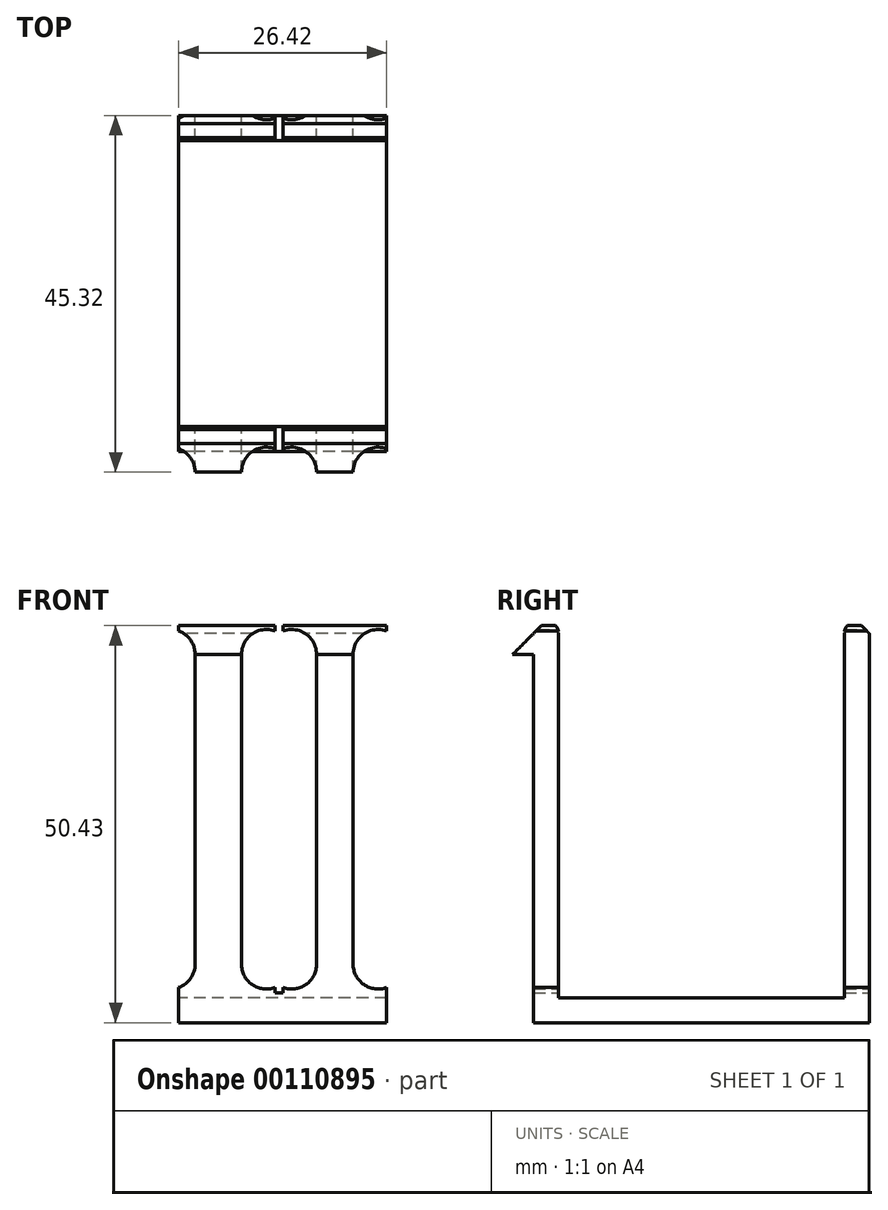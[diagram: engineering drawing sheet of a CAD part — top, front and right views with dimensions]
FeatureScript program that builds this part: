
annotation { "Feature Type Name" : "Feature", "Feature Type Description" : "" }
export const myFeature = defineFeature(function(context is Context, id is Id, definition is map)
    precondition{}
    {
        {
            var Q0;
            Q0=qCreatedBy(makeId("Right.planeOp"),FACE);
            var sketch = newSketch(context, id + "F0", { "sketchPlane" : qUnion([Q0])});
            skLineSegment(sketch, "E0", {"start": v(0, 49.53) * mm, "end": v(2.17, 50.43) * mm});
            skLineSegment(sketch, "E1", {"start": v(2.17, 50.43) * mm, "end": v(5.82, 46.78) * mm});
            skLineSegment(sketch, "E2", {"start": v(5.82, 46.78) * mm, "end": v(3.17, 46.78) * mm});
            skLineSegment(sketch, "E3", {"start": v(3.17, 46.78) * mm, "end": v(3.18, 0) * mm});
            skLineSegment(sketch, "E4", {"start": v(3.18, 0) * mm, "end": v(-18.16, 0) * mm});
            skLineSegment(sketch, "E5", {"start": v(-18.16, 0) * mm, "end": v(-18.16, 3.17) * mm});
            skLineSegment(sketch, "E6", {"start": v(-18.16, 3.17) * mm, "end": v(0, 3.17) * mm});
            skLineSegment(sketch, "E7", {"start": v(0, 3.18) * mm, "end": v(0, 49.53) * mm});
            skArc(sketch, "E8", {"start": v(2.17, 50.43) * mm, "mid": v(0.78, 50.7) * mm, "end": v(0, 49.53) * mm});
            skLineSegment(sketch, "E9.MirrorCS", {"start": v(-36.32, 49.53) * mm, "end": v(-38.5, 50.43) * mm});
            skArc(sketch, "E10.MirrorCS", {"start": v(-38.5, 50.43) * mm, "mid": v(-37.1, 50.7) * mm, "end": v(-36.32, 49.53) * mm});
            skLineSegment(sketch, "E11.MirrorCS", {"start": v(-36.32, 3.18) * mm, "end": v(-36.32, 49.53) * mm});
            skLineSegment(sketch, "E12.MirrorCS", {"start": v(-39.5, 46.78) * mm, "end": v(-39.5, 0) * mm});
            skLineSegment(sketch, "E13.MirrorCS", {"start": v(-18.16, 3.17) * mm, "end": v(-36.32, 3.17) * mm});
            skLineSegment(sketch, "E14.MirrorCS", {"start": v(-39.5, 0) * mm, "end": v(-18.16, 0) * mm});
            skLineSegment(sketch, "E15.MirrorCS", {"start": v(-38.5, 50.43) * mm, "end": v(-42.14, 46.78) * mm});
            skLineSegment(sketch, "E16.MirrorCS", {"start": v(-42.14, 46.78) * mm, "end": v(-39.5, 46.78) * mm});
            skSolve(sketch);
        }
        {
            var Q0;
            Q0 = qSketchRegion(id + "F0", true);
            extrude(context, id + "F1", {"entities" : qUnion([Q0]), "depth" : 191 * mm});
        }
        {
            var Q0;
            Q0=makeQuery(id+"F1.opExtrude","SWEPT_FACE",FACE,{"disambiguationData":[OSD([sQuery(id+"F0.wireOp",EDGE,"E3")])]});
            var sketch = newSketch(context, id + "F2", { "sketchPlane" : qUnion([Q0])});
            skLineSegment(sketch, "E17", {"start": v(0, 0) * mm, "end": v(-26.42, 0) * mm});
            skLineSegment(sketch, "E18", {"start": v(-26.42, 0) * mm, "end": v(0, 0) * mm});
            skLineSegment(sketch, "E19", {"start": v(0, 0) * mm, "end": v(0, 4.47) * mm});
            skLineSegment(sketch, "E20", {"start": v(-2.08, 7.45) * mm, "end": v(-2.08, 46.78) * mm});
            skLineSegment(sketch, "E21", {"start": v(-7.96, 7.45) * mm, "end": v(-7.96, 46.78) * mm});
            skLineSegment(sketch, "E22", {"start": v(-17.52, 7.45) * mm, "end": v(-17.52, 46.78) * mm});
            skLineSegment(sketch, "E23", {"start": v(-22.15, 7.45) * mm, "end": v(-22.15, 46.78) * mm});
            skArc(sketch, "E24", {"start": v(-2.08, 7.45) * mm, "mid": v(-1.5, 5.63) * mm, "end": v(0, 4.47) * mm});
            skArc(sketch, "E25", {"start": v(-26.42, 4.47) * mm, "mid": v(-23.5, 4.84) * mm, "end": v(-22.15, 7.45) * mm});
            skLineSegment(sketch, "E26", {"start": v(-26.42, 4.47) * mm, "end": v(-26.42, 0) * mm});
            skLineSegment(sketch, "E27", {"start": v(-13.25, 4.47) * mm, "end": v(-13.25, 3.8) * mm});
            skLineSegment(sketch, "E28", {"start": v(-13.25, 3.8) * mm, "end": v(-12.23, 3.8) * mm});
            skLineSegment(sketch, "E29", {"start": v(-12.23, 3.8) * mm, "end": v(-12.23, 4.47) * mm});
            skArc(sketch, "E30", {"start": v(-17.52, 7.45) * mm, "mid": v(-16.16, 4.84) * mm, "end": v(-13.25, 4.47) * mm});
            skArc(sketch, "E31", {"start": v(-12.23, 4.47) * mm, "mid": v(-9.32, 4.84) * mm, "end": v(-7.96, 7.45) * mm});
            skArc(sketch, "E32", {"start": v(-13.25, 49.76) * mm, "mid": v(-16.16, 49.38) * mm, "end": v(-17.52, 46.78) * mm});
            skArc(sketch, "E33", {"start": v(-7.96, 46.78) * mm, "mid": v(-9.32, 49.38) * mm, "end": v(-12.23, 49.76) * mm});
            skPoint(sketch, "E33.endSnap0", {"position": v(-16.27, 48.67) * mm});
            skArc(sketch, "E34", {"start": v(-22.15, 46.78) * mm, "mid": v(-23.5, 49.38) * mm, "end": v(-26.42, 49.76) * mm});
            skArc(sketch, "E35", {"start": v(0, 49.76) * mm, "mid": v(-1.5, 48.6) * mm, "end": v(-2.08, 46.78) * mm});
            skLineSegment(sketch, "E36", {"start": v(-26.42, 50.43) * mm, "end": v(-13.25, 50.43) * mm});
            skLineSegment(sketch, "E37", {"start": v(-13.25, 50.43) * mm, "end": v(-13.25, 49.76) * mm});
            skLineSegment(sketch, "E38", {"start": v(-26.42, 49.76) * mm, "end": v(-26.42, 50.43) * mm});
            skLineSegment(sketch, "E39", {"start": v(-12.23, 49.76) * mm, "end": v(-12.23, 50.43) * mm});
            skLineSegment(sketch, "E40", {"start": v(-12.23, 50.43) * mm, "end": v(0, 50.43) * mm});
            skLineSegment(sketch, "E41", {"start": v(0, 50.43) * mm, "end": v(0, 49.76) * mm});
            skLineSegment(sketch, "E42", {"start": v(-13.25, 50.43) * mm, "end": v(-12.23, 50.43) * mm, "construction": true});
            skLineSegment(sketch, "E43", {"start": v(-13.25, 49.76) * mm, "end": v(-12.23, 49.76) * mm, "construction": true});
            skSolve(sketch);
        }
        {
            var Q0;
            Q0 = qSketchRegion(id + "F2", true);
            extrude(context, id + "F3", {"entities" : qUnion([Q0]), "operationType" : NewBodyOperationType.INTERSECT, "endBound" : BoundingType.THROUGH_ALL, "oppositeDirection" : true, "depth" : 25.4 * mm});
        }
    });
